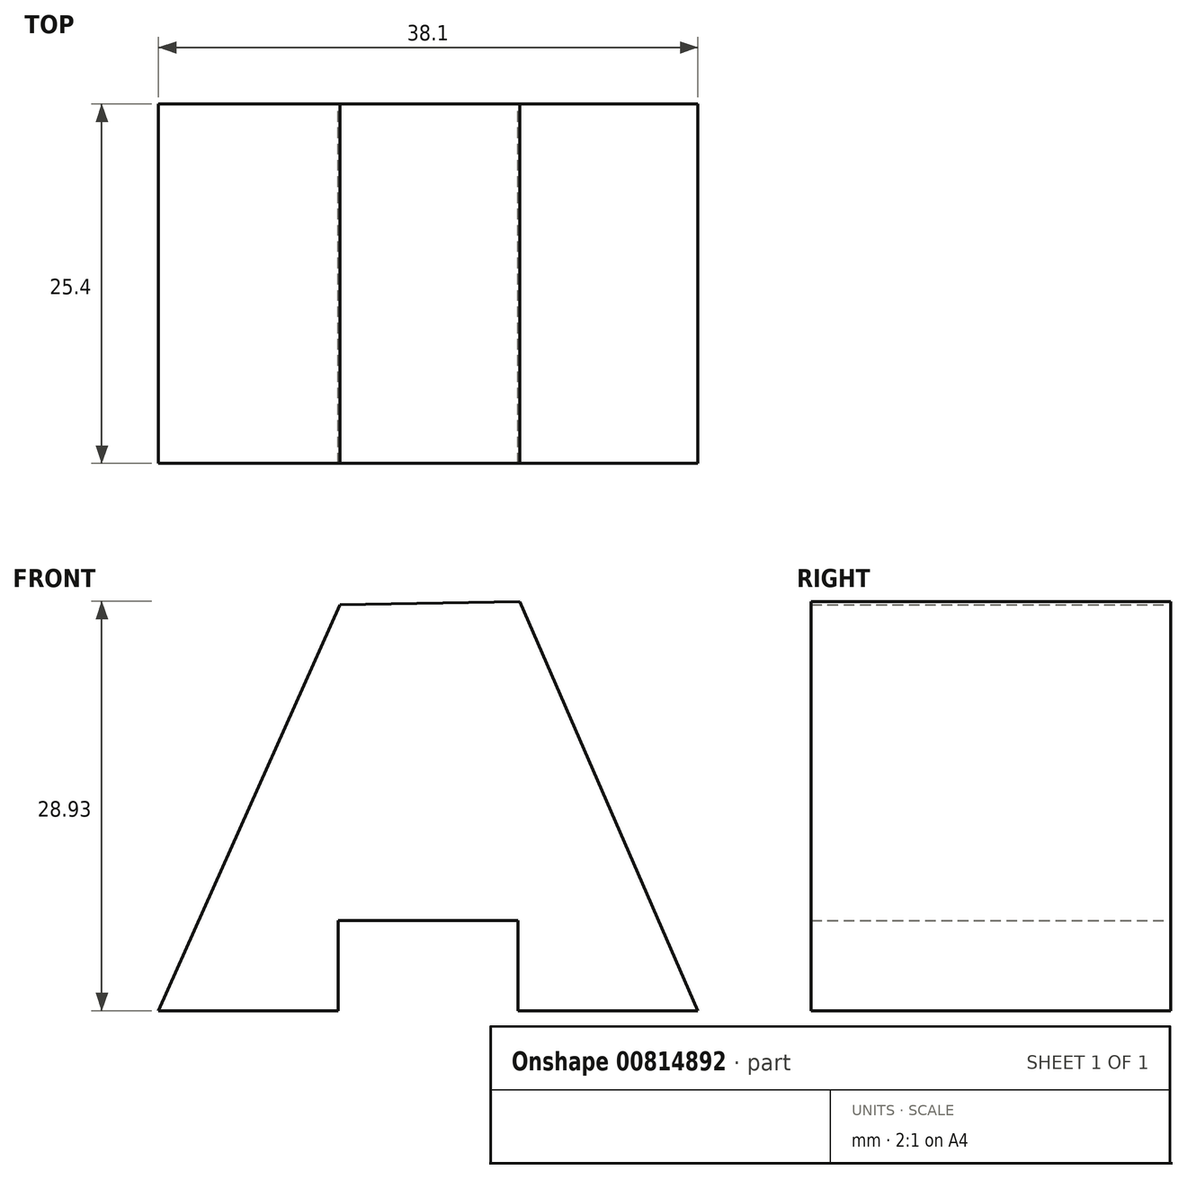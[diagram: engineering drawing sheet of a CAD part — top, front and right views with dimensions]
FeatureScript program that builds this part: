
annotation { "Feature Type Name" : "Feature", "Feature Type Description" : "" }
export const myFeature = defineFeature(function(context is Context, id is Id, definition is map)
    precondition{}
    {
        {
            var Q0;
            Q0=qCreatedBy(makeId("Front.planeOp"),FACE);
            var sketch = newSketch(context, id + "F0", { "sketchPlane" : qUnion([Q0])});
            skLineSegment(sketch, "E0", {"start": v(0, 0) * mm, "end": v(-12.7, 0) * mm});
            skLineSegment(sketch, "E1", {"start": v(-12.7, 0) * mm, "end": v(-12.7, 6.36) * mm});
            skLineSegment(sketch, "E2", {"start": v(-12.7, 6.36) * mm, "end": v(-25.4, 6.36) * mm});
            skLineSegment(sketch, "E3", {"start": v(-25.4, 6.36) * mm, "end": v(-25.4, 0) * mm});
            skLineSegment(sketch, "E4", {"start": v(-25.4, 0) * mm, "end": v(-38.1, 0) * mm});
            skLineSegment(sketch, "E5", {"start": v(-25.27, 28.69) * mm, "end": v(-12.58, 28.93) * mm});
            skLineSegment(sketch, "E6", {"start": v(-25.27, 28.69) * mm, "end": v(-38.1, 0) * mm});
            skLineSegment(sketch, "E7", {"start": v(-12.58, 28.93) * mm, "end": v(0, 0) * mm});
            skSolve(sketch);
        }
        {
            var Q0;
            Q0=makeQuery(id+"F0.imprint","IMPRINT",FACE,{"disambiguationData":[TD([[makeQuery(id+"F0.imprint","IMPRINT",EDGE,{"derivedFrom":sQuery(id+"F0.wireOp",EDGE,"E0")}),-1.0]])]});
            extrude(context, id + "F1", {"entities" : qUnion([Q0]), "depth" : 25.4 * mm, "offsetDistance" : 25.4 * mm});
        }
    });
